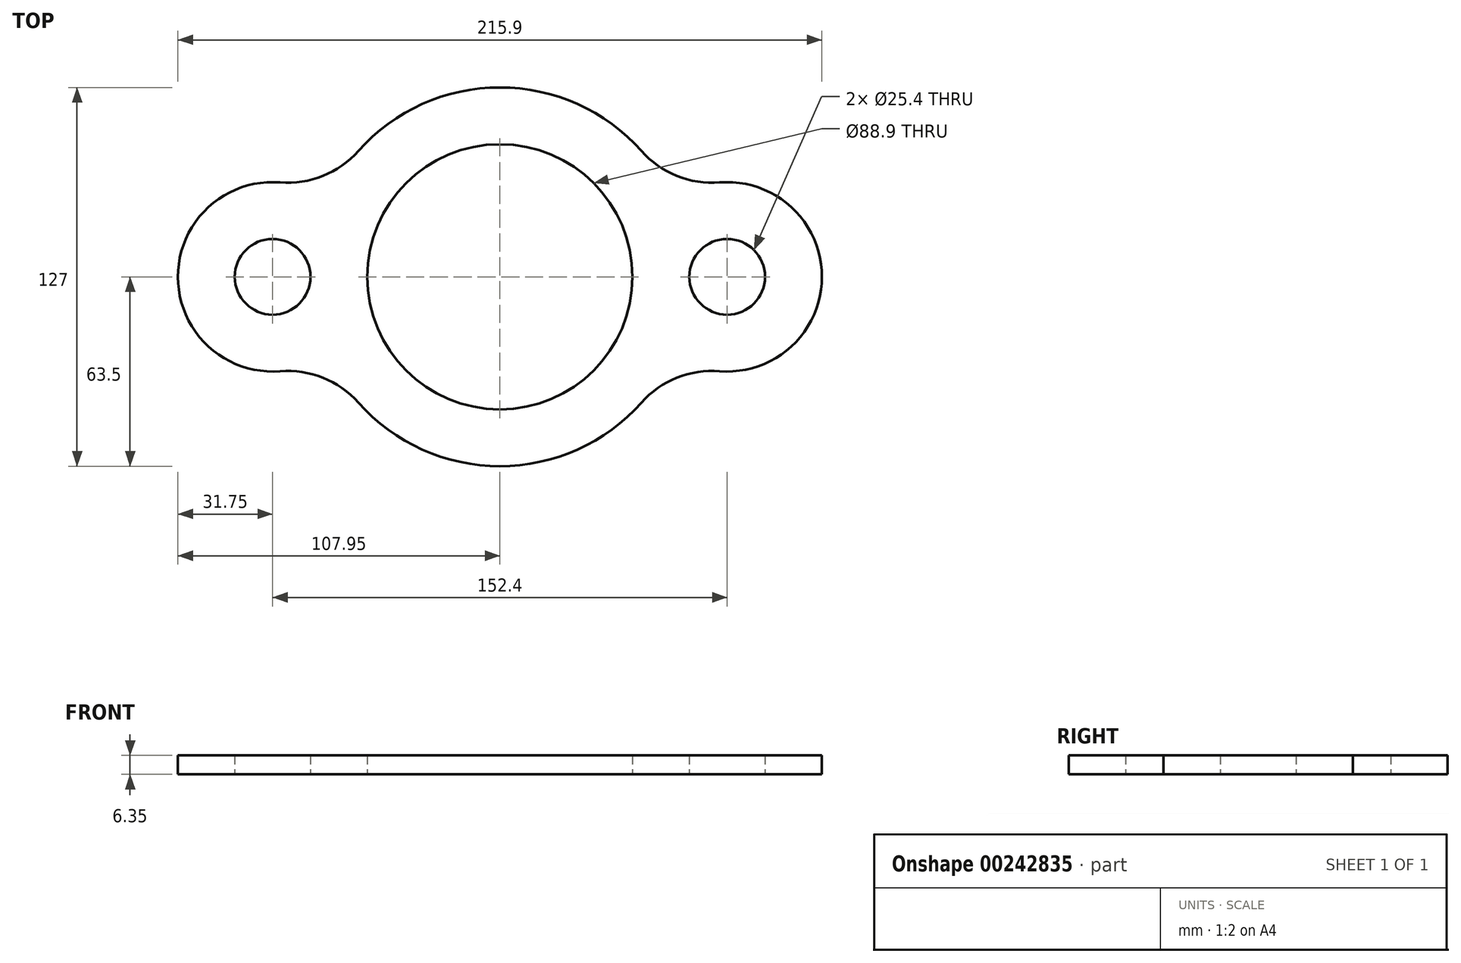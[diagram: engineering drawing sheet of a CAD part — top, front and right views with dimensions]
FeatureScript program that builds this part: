
annotation { "Feature Type Name" : "Feature", "Feature Type Description" : "" }
export const myFeature = defineFeature(function(context is Context, id is Id, definition is map)
    precondition{}
    {
        {
            var Q0;
            Q0=qCreatedBy(makeId("Top.planeOp"),FACE);
            var sketch = newSketch(context, id + "F0", { "sketchPlane" : qUnion([Q0])});
            skArc(sketch, "E0", {"start": v(-47.45, -42.2) * mm, "mid": v(0, -63.5) * mm, "end": v(47.45, -42.2) * mm});
            skCircle(sketch, "E1", {"center": v(0, 0) * mm, "radius": 44.45 * mm});
            skArc(sketch, "E2", {"start": v(73.69, -31.65) * mm, "mid": v(107.95, 0) * mm, "end": v(73.69, 31.65) * mm});
            skCircle(sketch, "E3", {"center": v(76.2, 0) * mm, "radius": 12.7 * mm});
            skArc(sketch, "E4", {"start": v(-73.69, 31.65) * mm, "mid": v(-107.95, 0) * mm, "end": v(-73.69, -31.65) * mm});
            skCircle(sketch, "E5", {"center": v(-76.2, 0) * mm, "radius": 12.7 * mm});
            skArc(sketch, "E6.trimOffspring", {"start": v(47.45, 42.2) * mm, "mid": v(0, 63.5) * mm, "end": v(-47.45, 42.2) * mm});
            skPoint(sketch, "E7.visualSharp", {"position": v(-57.94, 25.98) * mm});
            skArc(sketch, "E7.filletArc", {"start": v(-73.69, 31.65) * mm, "mid": v(-59.33, 33.84) * mm, "end": v(-47.45, 42.2) * mm});
            skPoint(sketch, "E8.visualSharp", {"position": v(57.94, 25.98) * mm});
            skArc(sketch, "E8.filletArc", {"start": v(47.45, 42.2) * mm, "mid": v(59.33, 33.84) * mm, "end": v(73.69, 31.65) * mm});
            skPoint(sketch, "E9.visualSharp", {"position": v(57.94, -25.98) * mm});
            skArc(sketch, "E9.filletArc", {"start": v(73.69, -31.65) * mm, "mid": v(59.33, -33.84) * mm, "end": v(47.45, -42.2) * mm});
            skPoint(sketch, "E10.visualSharp", {"position": v(-57.94, -25.98) * mm});
            skArc(sketch, "E10.filletArc", {"start": v(-47.45, -42.2) * mm, "mid": v(-59.33, -33.84) * mm, "end": v(-73.69, -31.65) * mm});
            skSolve(sketch);
        }
        {
            var Q0;
            Q0=makeQuery(id+"F0.imprint","IMPRINT",FACE,{"disambiguationData":[TD([[makeQuery(id+"F0.imprint","IMPRINT",EDGE,{"derivedFrom":sQuery(id+"F0.wireOp",EDGE,"E0")}),1.0]])]});
            extrude(context, id + "F1", {"entities" : qUnion([Q0]), "depth" : 6.35 * mm});
        }
    });
